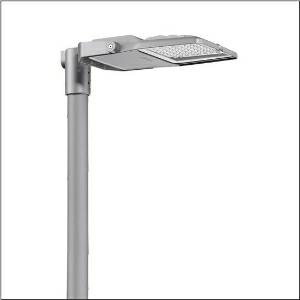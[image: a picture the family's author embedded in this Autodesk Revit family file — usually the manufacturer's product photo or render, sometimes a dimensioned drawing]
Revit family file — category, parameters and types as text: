
# Revit family: floodlight_fl_21_mini___pl61_5xa7775b2c3a_8a89
name_source: partatom
category: Lighting Fixtures
units: mm (PartAtom-declared; Revit-internal decimal feet)

## family parameters
Cut with Voids When Loaded = No
Host = Face
Light Source = No
Part Type = Normal
Room Calculation Point = No
Round Connector Dimension = Use Diameter
Shared = No

## types (1)
- --- (1 x LED, 6110 lm, 45.7 W, 3000K)
    Apparent Load = 46 VA
    CIE Flux Codes = 33 65 98 100 100
    Color Rendering = 70
    Color Temperature = 3000K
    Default Elevation = 1800 mm
    Description = Floodlight FL 21 mini, floodlight, primary light control with lens, of PMMA, primary optical cover: protective disc, of toughened safety glass, transparent, light distribution: PL61, light emission: direct distribution, installation type: surface-mounted, LED, High Power LED, rated luminous flux: 6.110lm, luminous efficacy: 134lm/W, light colour: 730, colour temperature: 3000K, control gear: Smart Interface (Zhaga), control: flexible luminous flux parameterisation, time-dependent luminous flux control, constant luminous flux control, overheat protection, pre-setting: logarithmic dimming characteristic, with terminal, 6-pole, mains connection: 220..240V, AC, 50/60Hz, start of lifetime: 46W, end of service life: 48W, reduction: 22W, luminaire housing, of diecast aluminium, powder-coated, Siteco® metallic grey (DB 702S), corrosivity category C5 mid according to DIN EN ISO 12944, suitable for swimming pools, chlorine-resistant, sealing non-destructively replaceable, please order mast flange separately, mast bracket, of steel, galvanised, powder-coated, Siteco® metallic grey (DB 702S), Smart Interface above, protection rating (complete): IP66, insulation class (complete): insulation class II (safety insulation), certification: CE, ENEC, VDE, protection symbol: D, impact resistance: IK08, permissible operating ambient temperature: -40..+40°C, permissible operating ambient temperature for outdoor applications: -40..+50°C, standard: DIN EN 12944, LABS conformity tested according to VDMA 24364:2018-05, packaging unit: 1 piece

Light Distribution: PL61
    Height = 70 mm
    Lamp = 1 x LED
    Lamp Light Flux = 6110 lm
    Lamp Power = 45.7 W
    Lamp count = 1
    Length = 485 mm
    Luminous efficacy = 134 lm/W
    Manufacturer = Siteco
    ModVariant = No
    Model = 5XA7775B2C3A
    Number of Poles = 1
    OnlyDefault = Yes
    Power Factor = 1
    Product Name = Floodlight FL 21 mini | PL61
    Product group = floodlight | pylon annexe
    ProductGroupID = 6200
    Protection Class = Protection class II
    Protection Degree = IP 66
    RLX_Detail_Level = 1
    RLX_Emergency_Light_Flux = 0 lm
    RLX_Emergency_Type = 0
    RLX_Emergency_Type_DB = No
    RlxData = <blob elided: 101081 chars, md5=f9e2c3dd>
    Socket = socket
    Standby Power = 0 W
    System Light Flux = 6110 lm
    System Power = 46 W
    Type Comments = factory setting: luminous flux: 100 % | dim-lin: 254 | 463 mA
    Type Image = l_1007125.jpg
    URL = http://relux.com
    VarID = @adj_172194
    Voltage = 0 V
    Weight = 0.00 kg
    Width = 337 mm

## geometry (parser evidence)
native form markers: Blend x4, Sweep x14
no freeform markers — native parametric forms only
